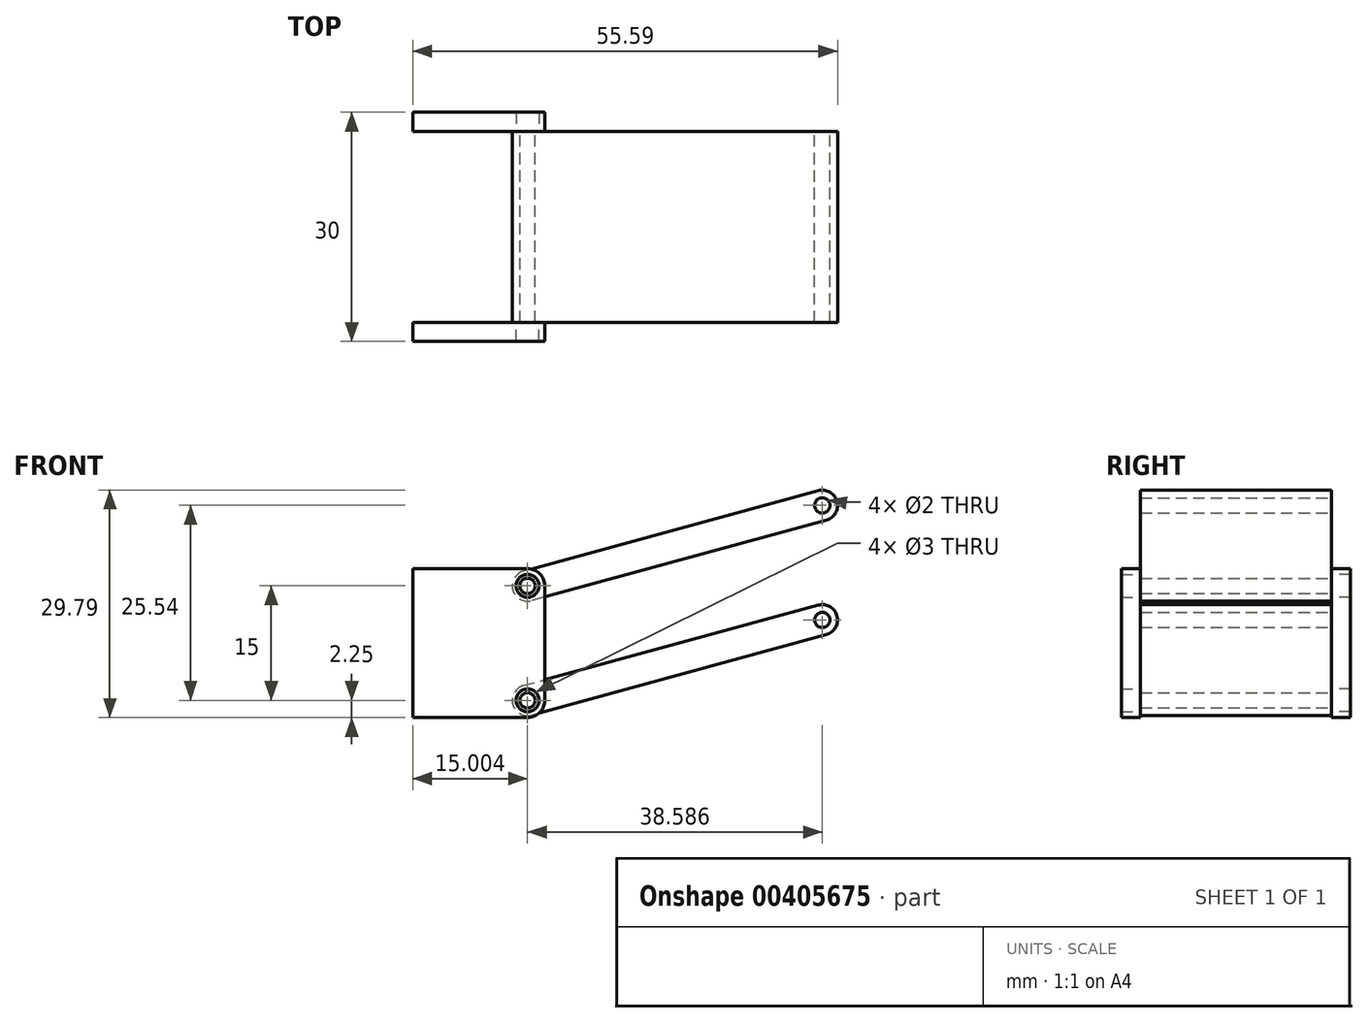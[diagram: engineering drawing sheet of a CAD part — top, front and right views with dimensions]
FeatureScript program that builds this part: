
annotation { "Feature Type Name" : "Feature", "Feature Type Description" : "" }
export const myFeature = defineFeature(function(context is Context, id is Id, definition is map)
    precondition{}
    {
        {
            var Q0;
            Q0=qCreatedBy(makeId("Top.planeOp"),FACE);
            var sketch = newSketch(context, id + "F0", { "sketchPlane" : qUnion([Q0])});
            skLineSegment(sketch, "E0", {"start": v(0, 85) * mm, "end": v(0, -85) * mm});
            skLineSegment(sketch, "E1", {"start": v(-70, 85) * mm, "end": v(70, 85) * mm});
            skLineSegment(sketch, "E2", {"start": v(-70, -85) * mm, "end": v(70, -85) * mm});
            skSolve(sketch);
        }
        {
            var Q0;
            Q0=sQuery(id+"F0.wireOp",EDGE,"E2");
            cPoint(context, id + "F1", {"entities" : qUnion([Q0]), "parameter" : 0.5});
        }
        {
            var Q0;
            Q0 = qCreatedBy(id + "F1" ,VERTEX);
            var Q1;
            Q1=qCreatedBy(makeId("Front.planeOp"),FACE);
            cPlane(context, id + "F2", {"entities" : qUnion([Q0, Q1]), "cplaneType" : CPlaneType.PLANE_POINT, "offset" : 25 * mm, "width" : 150 * mm, "height" : 150 * mm});
        }
        {
            var Q0;
            Q0=qCreatedBy(id+"F2.planeOp",FACE);
            var sketch = newSketch(context, id + "F3", { "sketchPlane" : qUnion([Q0])});
            skLineSegment(sketch, "E3", {"start": v(-15, 0) * mm, "end": v(15, 0) * mm});
            skLineSegment(sketch, "E4", {"start": v(-15, 0) * mm, "end": v(-55, 0) * mm});
            skLineSegment(sketch, "E5", {"start": v(-55, 0) * mm, "end": v(-70, 0) * mm});
            skLineSegment(sketch, "E6", {"start": v(15, 0) * mm, "end": v(55, 0) * mm});
            skLineSegment(sketch, "E7", {"start": v(55, 0) * mm, "end": v(70, 0) * mm});
            skSolve(sketch);
        }
        {
            var Q0;
            Q0=qCreatedBy(makeId("Top.planeOp"),FACE);
            var sketch = newSketch(context, id + "F4", { "sketchPlane" : qUnion([Q0])});
            skLineSegment(sketch, "E8", {"start": v(-55, -72.5) * mm, "end": v(-55, -97.5) * mm});
            skLineSegment(sketch, "E9", {"start": v(-70, -72.5) * mm, "end": v(-70, -97.5) * mm});
            skLineSegment(sketch, "E10", {"start": v(-55, -72.5) * mm, "end": v(-70, -72.5) * mm});
            skLineSegment(sketch, "E11", {"start": v(-70, -97.5) * mm, "end": v(-55, -97.5) * mm});
            skSolve(sketch);
        }
        {
            var Q0;
            Q0=qCreatedBy(id+"F2.planeOp",FACE);
            var sketch = newSketch(context, id + "F5", { "sketchPlane" : qUnion([Q0])});
            skLineSegment(sketch, "E12", {"start": v(-15, 0) * mm, "end": v(-53.59, -10.54) * mm});
            skLineSegment(sketch, "E13", {"start": v(-53.59, -10.54) * mm, "end": v(-68.59, -10.54) * mm});
            skLineSegment(sketch, "E14", {"start": v(-15, 0) * mm, "end": v(-15, 15) * mm});
            skLineSegment(sketch, "E15", {"start": v(-15, 15) * mm, "end": v(-53.59, 4.46) * mm});
            skLineSegment(sketch, "E16", {"start": v(-53.59, 4.46) * mm, "end": v(-53.59, -10.54) * mm});
            skLineSegment(sketch, "E17", {"start": v(-53.59, 4.46) * mm, "end": v(-68.59, 4.46) * mm});
            skLineSegment(sketch, "E18", {"start": v(-68.59, 4.46) * mm, "end": v(-68.59, -10.54) * mm});
            skLineSegment(sketch, "E19", {"start": v(-5, 35) * mm, "end": v(-51.17, 5.12) * mm, "construction": true});
            skLineSegment(sketch, "E20.bottom", {"start": v(-94.59, 25.96) * mm, "end": v(-68.59, 25.96) * mm});
            skLineSegment(sketch, "E20.top", {"start": v(-94.59, -37.04) * mm, "end": v(-68.59, -37.04) * mm});
            skLineSegment(sketch, "E20.left", {"start": v(-94.59, 25.96) * mm, "end": v(-94.59, -37.04) * mm});
            skLineSegment(sketch, "E20.right", {"start": v(-68.59, 25.96) * mm, "end": v(-68.59, -37.04) * mm});
            skPoint(sketch, "E21", {"position": v(-68.59, -5.54) * mm});
            skLineSegment(sketch, "E22", {"start": v(0, 0) * mm, "end": v(0, 79.42) * mm, "construction": true});
            skLineSegment(sketch, "E23.MirrorCS", {"start": v(5, 35) * mm, "end": v(51.17, 5.12) * mm, "construction": true});
            skLineSegment(sketch, "E24.MirrorCS", {"start": v(15, 0) * mm, "end": v(15, 15) * mm});
            skLineSegment(sketch, "E25.MirrorCS", {"start": v(15, 15) * mm, "end": v(53.59, 4.46) * mm});
            skLineSegment(sketch, "E26.MirrorCS", {"start": v(15, 0) * mm, "end": v(53.59, -10.54) * mm});
            skLineSegment(sketch, "E27.MirrorCS", {"start": v(53.59, 4.46) * mm, "end": v(53.59, -10.54) * mm});
            skLineSegment(sketch, "E28.MirrorCS", {"start": v(53.59, 4.46) * mm, "end": v(68.59, 4.46) * mm});
            skLineSegment(sketch, "E29.MirrorCS", {"start": v(53.59, -10.54) * mm, "end": v(68.59, -10.54) * mm});
            skLineSegment(sketch, "E30.MirrorCS", {"start": v(68.59, 25.96) * mm, "end": v(68.59, -37.04) * mm});
            skLineSegment(sketch, "E31.MirrorCS", {"start": v(94.59, 25.96) * mm, "end": v(68.59, 25.96) * mm});
            skLineSegment(sketch, "E32.MirrorCS", {"start": v(94.59, 25.96) * mm, "end": v(94.59, -37.04) * mm});
            skLineSegment(sketch, "E33.MirrorCS", {"start": v(94.59, -37.04) * mm, "end": v(68.59, -37.04) * mm});
            skLineSegment(sketch, "E34.MirrorCS", {"start": v(68.59, 4.46) * mm, "end": v(68.59, -10.54) * mm});
            skSolve(sketch);
        }
        {
            var Q0;
            Q0=qCreatedBy(id+"F2.planeOp",FACE);
            var sketch = newSketch(context, id + "F6", { "sketchPlane" : qUnion([Q0])});
            skLineSegment(sketch, "E35.0", {"start": v(-15, 15) * mm, "end": v(-53.59, 4.46) * mm, "construction": true});
            skLineSegment(sketch, "E36.0", {"start": v(-14.47, 13.07) * mm, "end": v(-53.06, 2.53) * mm});
            skLineSegment(sketch, "E37.0", {"start": v(-15.53, 16.93) * mm, "end": v(-54.11, 6.39) * mm});
            skCircle(sketch, "E38", {"center": v(-15, 15) * mm, "radius": 1 * mm});
            skCircle(sketch, "E39", {"center": v(-53.59, 4.46) * mm, "radius": 1 * mm});
            skArc(sketch, "E40", {"start": v(-14.47, 13.07) * mm, "mid": v(-13.07, 15.53) * mm, "end": v(-15.53, 16.93) * mm});
            skArc(sketch, "E41", {"start": v(-54.11, 6.39) * mm, "mid": v(-55.52, 3.93) * mm, "end": v(-53.06, 2.53) * mm});
            skArc(sketch, "E42", {"start": v(-14.47, -1.93) * mm, "mid": v(-13.07, 0.53) * mm, "end": v(-15.53, 1.93) * mm});
            skArc(sketch, "E43", {"start": v(-54.11, -8.61) * mm, "mid": v(-55.52, -11.07) * mm, "end": v(-53.06, -12.47) * mm});
            skLineSegment(sketch, "E44.0", {"start": v(-15, 0) * mm, "end": v(-53.59, -10.54) * mm, "construction": true});
            skCircle(sketch, "E45", {"center": v(-53.59, -10.54) * mm, "radius": 1 * mm});
            skCircle(sketch, "E46", {"center": v(-15, 0) * mm, "radius": 1 * mm});
            skLineSegment(sketch, "E47", {"start": v(-54.11, -8.61) * mm, "end": v(-15.53, 1.93) * mm});
            skLineSegment(sketch, "E48", {"start": v(-53.06, -12.47) * mm, "end": v(-14.47, -1.93) * mm});
            skSolve(sketch);
        }
        {
            var Q0;
            Q0 = qSketchRegion(id + "F6", true);
            var Q1;
            Q1=sQuery(id+"F4.wireOp",VERTEX,"E11.end");
            var Q2;
            Q2=sQuery(id+"F4.wireOp",VERTEX,"E10.start");
            extrude(context, id + "F7", {"entities" : qUnion([Q0]), "endBound" : BoundingType.UP_TO_VERTEX, "endBoundEntityVertex" : qUnion([Q1]), "depth" : 25 * mm, "hasSecondDirection" : true, "secondDirectionBound" : BoundingType.UP_TO_VERTEX, "secondDirectionOppositeDirection" : true, "secondDirectionBoundEntityVertex" : qUnion([Q2]), "secondDirectionDepth" : 25 * mm});
        }
        {
            var Q0;
            Q0=makeQuery(id+"F7.opExtrude","CAP_FACE",FACE,{"disambiguationData":[OSD([sQuery(id+"F6.wireOp",EDGE,"E42"),sQuery(id+"F6.wireOp",EDGE,"E43"),sQuery(id+"F6.wireOp",EDGE,"E45"),sQuery(id+"F6.wireOp",EDGE,"E46"),sQuery(id+"F6.wireOp",EDGE,"E47"),sQuery(id+"F6.wireOp",EDGE,"E48")])],"isStart":false});
            var sketch = newSketch(context, id + "F8", { "sketchPlane" : qUnion([Q0])});
            skCircle(sketch, "E49.0", {"center": v(-53.59, 4.46) * mm, "radius": 1.5 * mm});
            skCircle(sketch, "E50.0", {"center": v(-53.59, -10.54) * mm, "radius": 1.5 * mm});
            skLineSegment(sketch, "E51", {"start": v(-68.59, 6.7) * mm, "end": v(-53.59, 6.7) * mm});
            skLineSegment(sketch, "E52", {"start": v(-51.34, 4.46) * mm, "end": v(-51.34, -10.54) * mm});
            skLineSegment(sketch, "E53", {"start": v(-53.59, -12.8) * mm, "end": v(-68.59, -12.8) * mm});
            skLineSegment(sketch, "E54", {"start": v(-68.59, -12.8) * mm, "end": v(-68.59, 6.7) * mm});
            skArc(sketch, "E55", {"start": v(-51.34, 4.46) * mm, "mid": v(-52, 6.05) * mm, "end": v(-53.59, 6.7) * mm});
            skArc(sketch, "E56", {"start": v(-53.59, -12.8) * mm, "mid": v(-52, -12.13) * mm, "end": v(-51.34, -10.54) * mm});
            skSolve(sketch);
        }
        {
            var Q0;
            Q0 = qSketchRegion(id + "F8", true);
            var Q1;
            Q1=makeQuery(id+"F7.opExtrude","CAP_FACE",FACE,{"disambiguationData":[OSD([sQuery(id+"F6.wireOp",EDGE,"E42"),sQuery(id+"F6.wireOp",EDGE,"E43"),sQuery(id+"F6.wireOp",EDGE,"E45"),sQuery(id+"F6.wireOp",EDGE,"E46"),sQuery(id+"F6.wireOp",EDGE,"E47"),sQuery(id+"F6.wireOp",EDGE,"E48")])],"isStart":false});
            var Q2;
            Q2=makeQuery(id+"F7.opExtrude","CAP_FACE",FACE,{"disambiguationData":[OSD([sQuery(id+"F6.wireOp",EDGE,"E36.0"),sQuery(id+"F6.wireOp",EDGE,"E37.0"),sQuery(id+"F6.wireOp",EDGE,"E38"),sQuery(id+"F6.wireOp",EDGE,"E39"),sQuery(id+"F6.wireOp",EDGE,"E40"),sQuery(id+"F6.wireOp",EDGE,"E41")])],"isStart":true});
            extrude(context, id + "F9", {"entities" : qUnion([Q0]), "endBoundEntityFace" : qUnion([Q1]), "depth" : 2.5 * mm});
        }
        {
            var Q0;
            Q0=makeQuery(id+"F7.opExtrude","CAP_FACE",FACE,{"disambiguationData":[OSD([sQuery(id+"F6.wireOp",EDGE,"E36.0"),sQuery(id+"F6.wireOp",EDGE,"E37.0"),sQuery(id+"F6.wireOp",EDGE,"E38"),sQuery(id+"F6.wireOp",EDGE,"E39"),sQuery(id+"F6.wireOp",EDGE,"E40"),sQuery(id+"F6.wireOp",EDGE,"E41")])],"isStart":true});
            var sketch = newSketch(context, id + "F10", { "sketchPlane" : qUnion([Q0])});
            skCircle(sketch, "E57.0", {"center": v(53.59, 4.46) * mm, "radius": 1.5 * mm});
            skCircle(sketch, "E57.1", {"center": v(53.59, -10.54) * mm, "radius": 1.5 * mm});
            skLineSegment(sketch, "E57.2", {"start": v(68.59, 6.7) * mm, "end": v(53.59, 6.7) * mm});
            skLineSegment(sketch, "E57.3", {"start": v(51.34, 4.46) * mm, "end": v(51.34, -10.54) * mm});
            skLineSegment(sketch, "E57.4", {"start": v(53.59, -12.8) * mm, "end": v(68.59, -12.8) * mm});
            skLineSegment(sketch, "E57.5", {"start": v(68.59, -12.8) * mm, "end": v(68.59, 6.7) * mm});
            skArc(sketch, "E57.6", {"start": v(51.34, 4.46) * mm, "mid": v(52, 6.05) * mm, "end": v(53.59, 6.7) * mm});
            skArc(sketch, "E57.7", {"start": v(53.59, -12.8) * mm, "mid": v(52, -12.13) * mm, "end": v(51.34, -10.54) * mm});
            skSolve(sketch);
        }
        {
            var Q0;
            Q0 = qSketchRegion(id + "F10", true);
            extrude(context, id + "F11", {"entities" : qUnion([Q0]), "depth" : 2.5 * mm});
        }
    });
